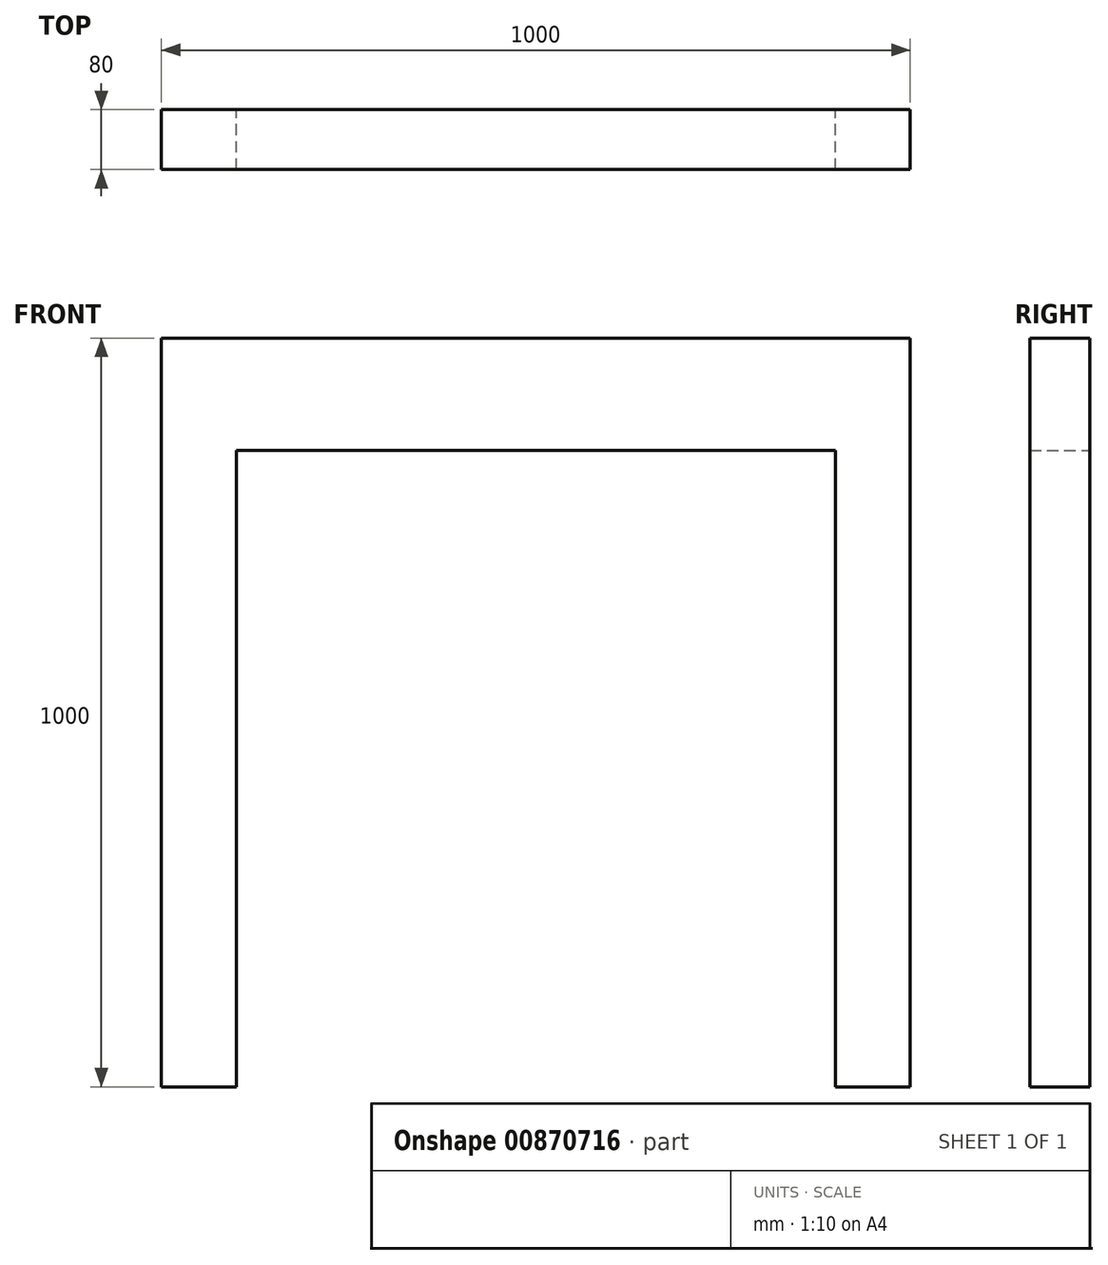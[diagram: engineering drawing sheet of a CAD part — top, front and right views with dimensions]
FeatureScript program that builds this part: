
annotation { "Feature Type Name" : "Feature", "Feature Type Description" : "" }
export const myFeature = defineFeature(function(context is Context, id is Id, definition is map)
    precondition{}
    {
        {
            var Q0;
            Q0=qCreatedBy(makeId("Front.planeOp"),FACE);
            var sketch = newSketch(context, id + "F0", { "sketchPlane" : qUnion([Q0])});
            skLineSegment(sketch, "E0.bottom", {"start": v(-500, 0) * mm, "end": v(500, 0) * mm});
            skLineSegment(sketch, "E0.top", {"start": v(-500, 1000) * mm, "end": v(500, 1000) * mm});
            skLineSegment(sketch, "E0.left", {"start": v(-500, 0) * mm, "end": v(-500, 1000) * mm});
            skLineSegment(sketch, "E0.right", {"start": v(500, 0) * mm, "end": v(500, 1000) * mm});
            skPoint(sketch, "E1", {"position": v(0, 0) * mm});
            skLineSegment(sketch, "E2", {"start": v(-400, 0) * mm, "end": v(-400, 850) * mm});
            skLineSegment(sketch, "E3", {"start": v(-400, 850) * mm, "end": v(400, 850) * mm});
            skLineSegment(sketch, "E4", {"start": v(400, 850) * mm, "end": v(400, 0) * mm});
            skSolve(sketch);
        }
        {
            var Q0;
            Q0=makeQuery(id+"F0.imprint","IMPRINT",FACE,{"disambiguationData":[TD([[makeQuery(id+"F0.imprint","IMPRINT",EDGE,{"derivedFrom":sQuery(id+"F0.wireOp",EDGE,"E0.top")}),-1.0]])]});
            var sketch = newSketch(context, id + "F1", { "sketchPlane" : qUnion([Q0])});
            skLineSegment(sketch, "E5.0", {"start": v(-400, 850) * mm, "end": v(400, 850) * mm});
            skLineSegment(sketch, "E6.0", {"start": v(-500, 1000) * mm, "end": v(500, 1000) * mm});
            skLineSegment(sketch, "E7.0", {"start": v(400, 850) * mm, "end": v(400, 0) * mm});
            skLineSegment(sketch, "E8.0", {"start": v(500, 0) * mm, "end": v(500, 1000) * mm});
            skLineSegment(sketch, "E9.0", {"start": v(-400, 0) * mm, "end": v(-400, 850) * mm});
            skLineSegment(sketch, "E10.0", {"start": v(-500, 0) * mm, "end": v(-500, 1000) * mm});
            skLineSegment(sketch, "E11.0", {"start": v(-500, 0) * mm, "end": v(-400, 0) * mm});
            skLineSegment(sketch, "E12.trimOffspring", {"start": v(400, 0) * mm, "end": v(500, 0) * mm});
            skSolve(sketch);
        }
        {
            var Q0;
            Q0 = qSketchRegion(id + "F1", true);
            extrude(context, id + "F2", {"entities" : qUnion([Q0]), "depth" : 80 * mm, "offsetDistance" : 25 * mm});
        }
    });
